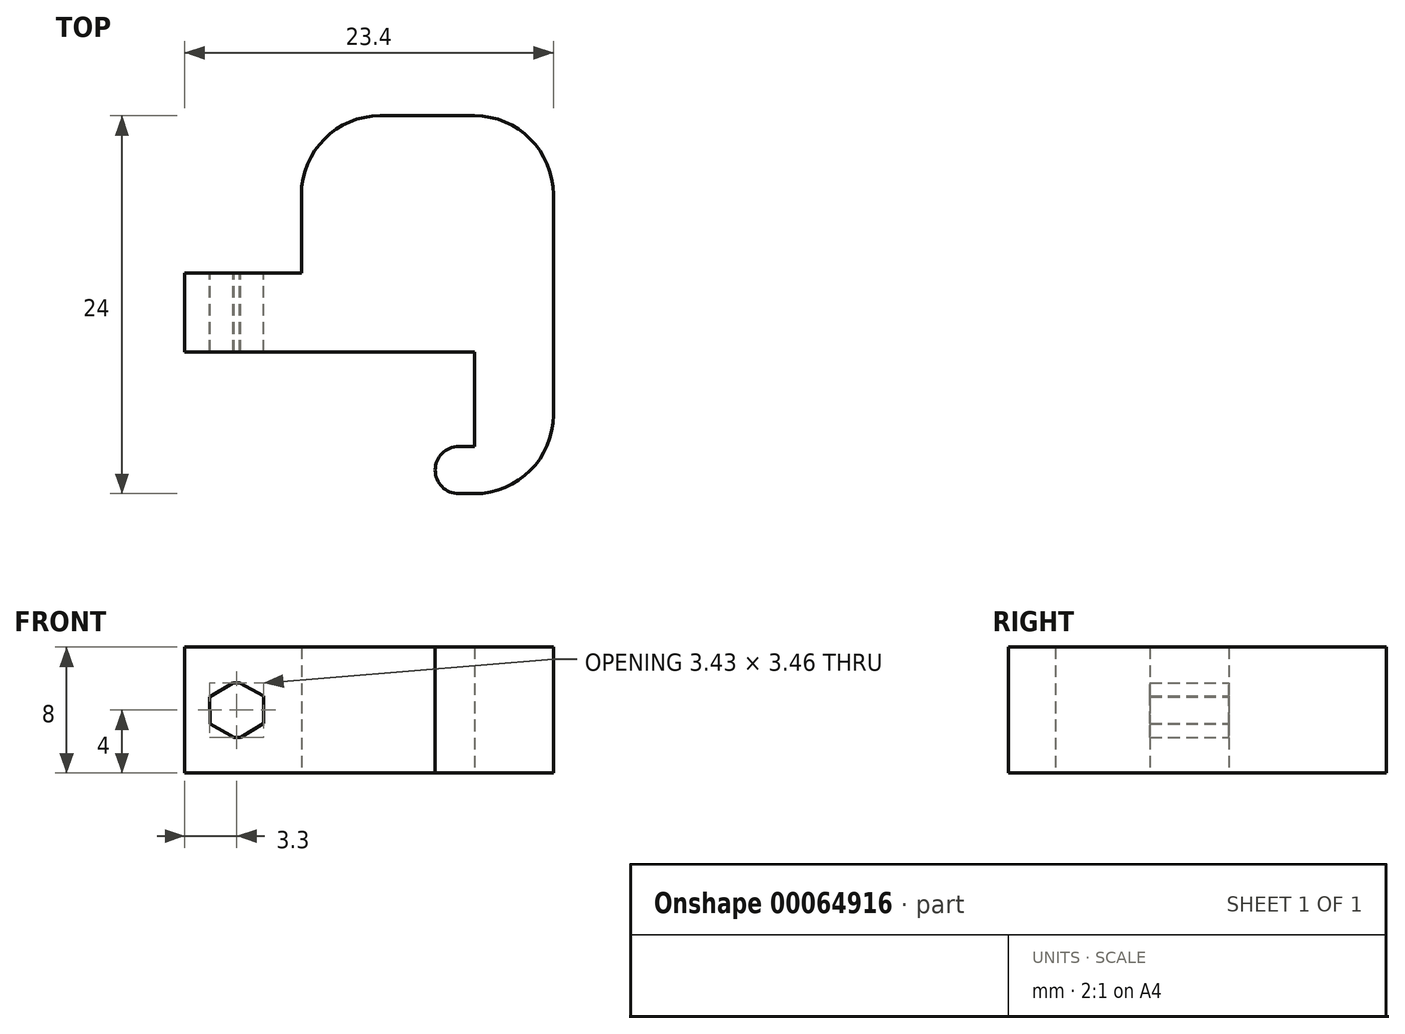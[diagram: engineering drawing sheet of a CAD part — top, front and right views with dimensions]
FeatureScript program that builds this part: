
annotation { "Feature Type Name" : "Feature", "Feature Type Description" : "" }
export const myFeature = defineFeature(function(context is Context, id is Id, definition is map)
    precondition{}
    {
        {
            var Q0;
            Q0=qCreatedBy(makeId("Top.planeOp"),FACE);
            var sketch = newSketch(context, id + "F0", { "sketchPlane" : qUnion([Q0])});
            skLineSegment(sketch, "E0", {"start": v(0, 0) * mm, "end": v(5, 0) * mm});
            skLineSegment(sketch, "E1", {"start": v(5, 0) * mm, "end": v(5, 14) * mm});
            skLineSegment(sketch, "E2", {"start": v(5, 14) * mm, "end": v(-18, 14) * mm});
            skLineSegment(sketch, "E3", {"start": v(-18, 14) * mm, "end": v(-18, 9) * mm});
            skLineSegment(sketch, "E4", {"start": v(-18, 9) * mm, "end": v(0, 9) * mm});
            skLineSegment(sketch, "E5", {"start": v(0, 9) * mm, "end": v(0, 3) * mm});
            skLineSegment(sketch, "E6", {"start": v(0, 3) * mm, "end": v(-1, 3) * mm});
            skLineSegment(sketch, "E7", {"start": v(0, 0) * mm, "end": v(-1, 0) * mm});
            skArc(sketch, "E8", {"start": v(-1, 3) * mm, "mid": v(-2.5, 1.5) * mm, "end": v(-1, 0) * mm});
            skSolve(sketch);
        }
        {
            var Q0;
            Q0=qSketchRegion(id+"F0",true);
            extrude(context, id + "F1", {"entities" : qUnion([Q0]), "depth" : 8 * mm});
        }
        {
            var Q0;
            Q0=makeQuery(id+"F1.opExtrude","SWEPT_FACE",FACE,{"disambiguationData":[OSD([sQuery(id+"F0.wireOp",EDGE,"E2")])]});
            var sketch = newSketch(context, id + "F2", { "sketchPlane" : qUnion([Q0])});
            skLineSegment(sketch, "E9", {"start": v(15.3, 8) * mm, "end": v(15.3, 0) * mm});
            skLineSegment(sketch, "E10.0", {"start": v(16.79, 3.1) * mm, "end": v(15.27, 2.27) * mm});
            skLineSegment(sketch, "E10.4", {"start": v(15.33, 5.73) * mm, "end": v(16.81, 4.84) * mm});
            skLineSegment(sketch, "E10.5", {"start": v(16.81, 4.84) * mm, "end": v(16.79, 3.1) * mm});
            skLineSegment(sketch, "E11.0", {"start": v(14.87, 2.27) * mm, "end": v(13.39, 3.16) * mm});
            skLineSegment(sketch, "E11.1", {"start": v(13.39, 3.16) * mm, "end": v(13.41, 4.9) * mm});
            skLineSegment(sketch, "E11.2", {"start": v(13.41, 4.9) * mm, "end": v(14.93, 5.73) * mm});
            skLineSegment(sketch, "E12", {"start": v(14.93, 5.73) * mm, "end": v(15.33, 5.73) * mm});
            skLineSegment(sketch, "E13", {"start": v(14.87, 2.27) * mm, "end": v(15.27, 2.27) * mm});
            skSolve(sketch);
        }
        {
            var Q0;
            Q0=makeQuery(id+"F2.imprint","IMPRINT",FACE,{"disambiguationData":[TD([[makeQuery(id+"F2.imprint","IMPRINT",EDGE,{"derivedFrom":sQuery(id+"F2.wireOp",EDGE,"E11.0")}),-1.0]])]});
            var Q1;
            {var subQ0=sQuery(id+"F2.wireOp",EDGE,"E10.4");Q1=makeQuery(id+"F2.imprint","IMPRINT",FACE,{"disambiguationData":[TD([[makeQuery(id+"F2.imprint","IMPRINT",EDGE,{"derivedFrom":subQ0}),-1.0]])]});}
            extrude(context, id + "F3", {"entities" : qUnion([Q0, Q1]), "operationType" : NewBodyOperationType.REMOVE, "oppositeDirection" : true, "depth" : 25 * mm, "hasSecondDirection" : true, "secondDirectionOppositeDirection" : false, "secondDirectionDepth" : 25 * mm});
        }
        {
            var Q0;
            Q0=makeQuery(id+"F1.opExtrude","SWEPT_FACE",FACE,{"disambiguationData":[OSD([sQuery(id+"F0.wireOp",EDGE,"E2")])]});
            var sketch = newSketch(context, id + "F4", { "sketchPlane" : qUnion([Q0])});
            skLineSegment(sketch, "E14.bottom", {"start": v(-5, 8) * mm, "end": v(11, 8) * mm});
            skLineSegment(sketch, "E14.top", {"start": v(-5, 0) * mm, "end": v(11, 0) * mm});
            skLineSegment(sketch, "E14.left", {"start": v(-5, 8) * mm, "end": v(-5, 0) * mm});
            skLineSegment(sketch, "E14.right", {"start": v(11, 8) * mm, "end": v(11, 0) * mm});
            skSolve(sketch);
        }
        {
            var Q0;
            Q0=qSketchRegion(id+"F4",true);
            extrude(context, id + "F5", {"entities" : qUnion([Q0]), "operationType" : NewBodyOperationType.ADD, "depth" : 10 * mm});
        }
        {
            var Q0;
            Q0=makeQuery(id+"F5.opExtrude","CAP_EDGE",EDGE,{"disambiguationData":[OSD([sQuery(id+"F4.wireOp",EDGE,"E14.left")])],"isStart":false});
            var Q1;
            Q1=makeQuery(id+"F5.opExtrude","CAP_EDGE",EDGE,{"disambiguationData":[OSD([sQuery(id+"F4.wireOp",EDGE,"E14.right")])],"isStart":false});
            fillet(context, id + "F6", {"entities" : qUnion([Q0, Q1]), "radius" : 5 * mm, "tangentPropagation" : true, "allowEdgeOverflow" : false});
        }
        {
            var Q0;
            Q0=makeQuery(id+"F1.opExtrude","SWEPT_EDGE",EDGE,{"disambiguationData":[OSD([sQuery(id+"F0.wireOp",EDGE,"E0"),sQuery(id+"F0.wireOp",EDGE,"E1")])]});
            fillet(context, id + "F7", {"entities" : qUnion([Q0]), "radius" : 5 * mm, "tangentPropagation" : true, "allowEdgeOverflow" : false});
        }
        {
            var Q0;
            Q0=makeQuery(id+"F1.opExtrude","SWEPT_FACE",FACE,{"disambiguationData":[OSD([sQuery(id+"F0.wireOp",EDGE,"E3")])]});
            extrude(context, id + "F8", {"entities" : qUnion([Q0]), "operationType" : NewBodyOperationType.ADD, "depth" : .4 * mm});
        }
    });
